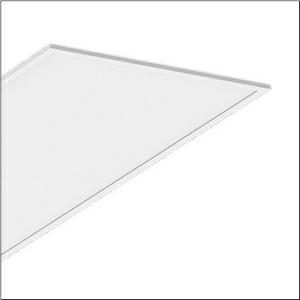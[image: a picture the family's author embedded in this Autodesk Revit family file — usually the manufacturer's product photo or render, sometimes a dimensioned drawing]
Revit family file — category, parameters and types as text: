
# Revit family: apollon_21_linear_51mq1awd2m14
name_source: partatom
category: Lighting Fixtures
units: mm (PartAtom-declared; Revit-internal decimal feet)

## family parameters
Cut with Voids When Loaded = No
Host = Face
Light Source = No
Part Type = Normal
Room Calculation Point = No
Round Connector Dimension = Use Diameter
Shared = No

## types (1)
- --- (1 x LED, 7000 lm, 44.5 W, 4000K)
    Apparent Load = 45 VA
    CIE Flux Codes = 60 87 97 100 100
    Color Rendering = 80
    Color Temperature = 4000K
    Default Elevation = 1800 mm
    Description = Apollon 21 linear, office luminaire, primary optical cover: micro prismatic cover, of PMMA, CAT 2 (L<= 3000cd/m²), light emission: direct distribution, primary light characteristic: symmetric, installation type: lay-in mounting, LED, rated luminous flux: 7.820lm, luminous efficacy: 173lm/W, light colour: 830/840, colour temperature: 3000/4000K, control gear: DALI 2, Multilumen, with terminal, 5-pole, mains connection: 220..240V, AC/DC, 0/50..60Hz, rated input power: 45.3W, housing, of aluminium, coated, traffic white (RAL 9016), length: 1.195mm, width: 595mm, height: 55mm, recess depth: 180mm, housing upper side, of sheet steel, galvanised, protection rating (complete): IP20, protection rating (lamp compartment, on room side): IP50, insulation class (complete): insulation class II (safety insulation), certification: CE, ENEC, impact resistance: IK03, permissible operating ambient temperature: -20..+45°C, permissible storage temperature: -40..+80°C, standard: EN 60598-2-22, packaging unit: 1 piece
    Height = 0 mm  [stored 0 ft]
    Lamp = 1 x LED
    Lamp Light Flux = 7000 lm
    Lamp Power = 44.5 W
    Lamp count = 1
    Length = 1195 mm
    Luminous efficacy = 157 lm/W
    Manufacturer = Siteco
    ModVariant = No
    Model = 51MQ1AWD2M14
    Mounting Place = Ceiling
    Mounting Type = Recessed
    Number of Poles = 1
    OnlyDefault = Yes
    Power Factor = 1
    Product Name = Apollon 21 linear
    Product group = office luminaire | ceiling recessed
    ProductGroupID = 401
    Protection Class = Protection class II
    Protection Degree = IP 20
    RLX_Detail_Level = 1
    RLX_Emergency_Light_Flux = 0 lm
    RLX_Emergency_Type = 0
    RLX_Emergency_Type_DB = No
    RlxData = <blob elided: 19569 chars, md5=a147faa6>
    Socket = socket
    Standby Power = 0 W
    System Light Flux = 7000 lm
    System Power = 45 W
    Type Comments = factory setting
    Type Image = l_1335551.jpg
    URL = http://relux.com
    VarID = @adj_067502
    Voltage = 0 V
    Weight = 0.00 kg
    Width = 595 mm

note: [stored X ft] marks values corroborated as IEEE doubles in the binary element streams (Revit-internal decimal feet)

## geometry (parser evidence)
native form markers: Blend x4, Sweep x13
no freeform markers — native parametric forms only
